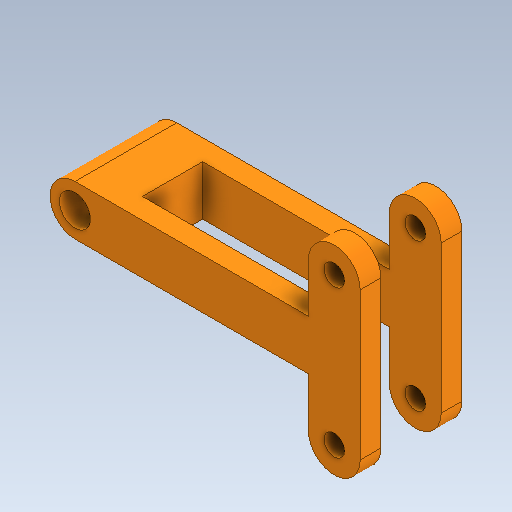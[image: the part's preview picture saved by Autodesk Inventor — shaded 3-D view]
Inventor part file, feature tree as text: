
AUTODESK INVENTOR PART (.ipt)
format: ipt  version: 2020 (Build 240168000, 168)  size: 197,120 bytes
history: native  units: in
note: dims shown in document units (in); Inventor stores cm internally (conversion verified against a paired STEP export)
features: extrude x3, sketch x3, projected_geometry x2, mirror x1
ambient origin geometry x8: Origin, YZ Plane, XZ Plane, XY Plane, X Axis, Y Axis, Z Axis, Center Point
bodies: Solid1 (feature_tree)
feature tree (9):
  extrude  "Extrusion1"  Depth=0.2797in
  extrude  "Extrusion2"  Depth=0.1969in
  extrude  "Extrusion4"  Depth=0.0787in
  mirror  "Mirror2"
  sketch  "Sketch1"  dims[d0=0.2797in d1=0.2797in]
  sketch  "Sketch2"  dims[d2=0.1969in d3=0.1969in]
  projected_geometry  "Projected Loop1"
  sketch  "Sketch4"  dims[d4=0.1969in d5=0.0787in d6=0.0787in d7=0.0945in d8=0.8071in d9=0.189in d10=0.0787in d11=0.0in d12=0.1144in d13=0.0in d21=0.0787in d22=0.1181in d23=0.189in d24=0.3937in d25=0.0in d26=0.0984in d18=0.0197in d19=0.0344in d20=0.0197in]
  projected_geometry  "Projected Loop3"
